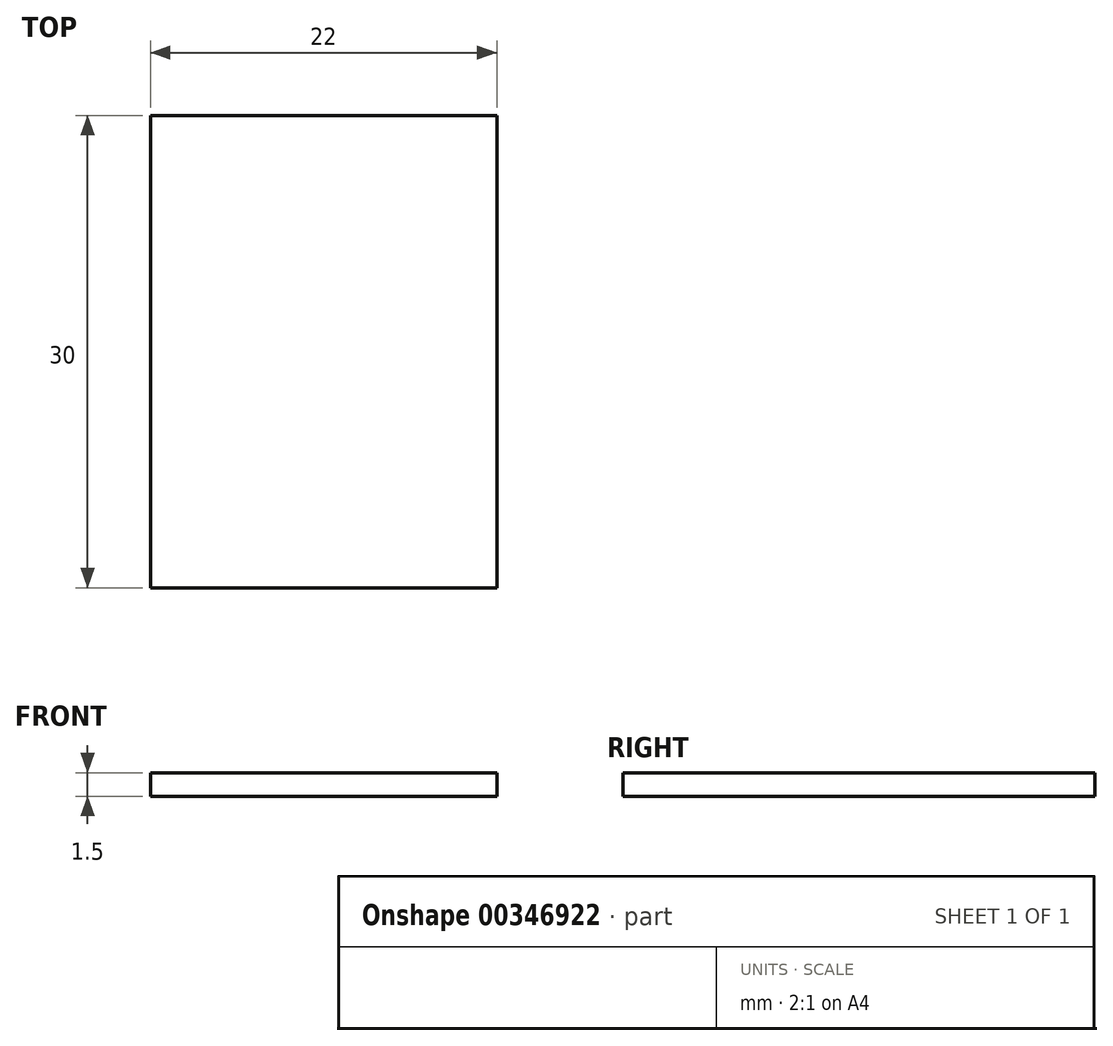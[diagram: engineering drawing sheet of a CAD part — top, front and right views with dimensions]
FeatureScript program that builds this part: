
annotation { "Feature Type Name" : "Feature", "Feature Type Description" : "" }
export const myFeature = defineFeature(function(context is Context, id is Id, definition is map)
    precondition{}
    {
        {
            var Q0;
            Q0=qCreatedBy(makeId("Top.planeOp"),FACE);
            var sketch = newSketch(context, id + "F0", { "sketchPlane" : qUnion([Q0])});
            skLineSegment(sketch, "E0.bottom", {"start": v(-12.09, -18.2) * mm, "end": v(9.91, -18.2) * mm});
            skLineSegment(sketch, "E0.top", {"start": v(-12.09, 11.8) * mm, "end": v(9.91, 11.8) * mm});
            skLineSegment(sketch, "E0.left", {"start": v(-12.09, -18.2) * mm, "end": v(-12.09, 11.8) * mm});
            skLineSegment(sketch, "E0.right", {"start": v(9.91, -18.2) * mm, "end": v(9.91, 11.8) * mm});
            skSolve(sketch);
        }
        {
            var Q0;
            Q0=makeQuery(id+"F0.imprint","IMPRINT",FACE,{"disambiguationData":[TD([[makeQuery(id+"F0.imprint","IMPRINT",EDGE,{"derivedFrom":sQuery(id+"F0.wireOp",EDGE,"E0.bottom")}),1.0]])]});
            extrude(context, id + "F1", {"entities" : qUnion([Q0]), "depth" : 1.5 * mm});
        }
    });
